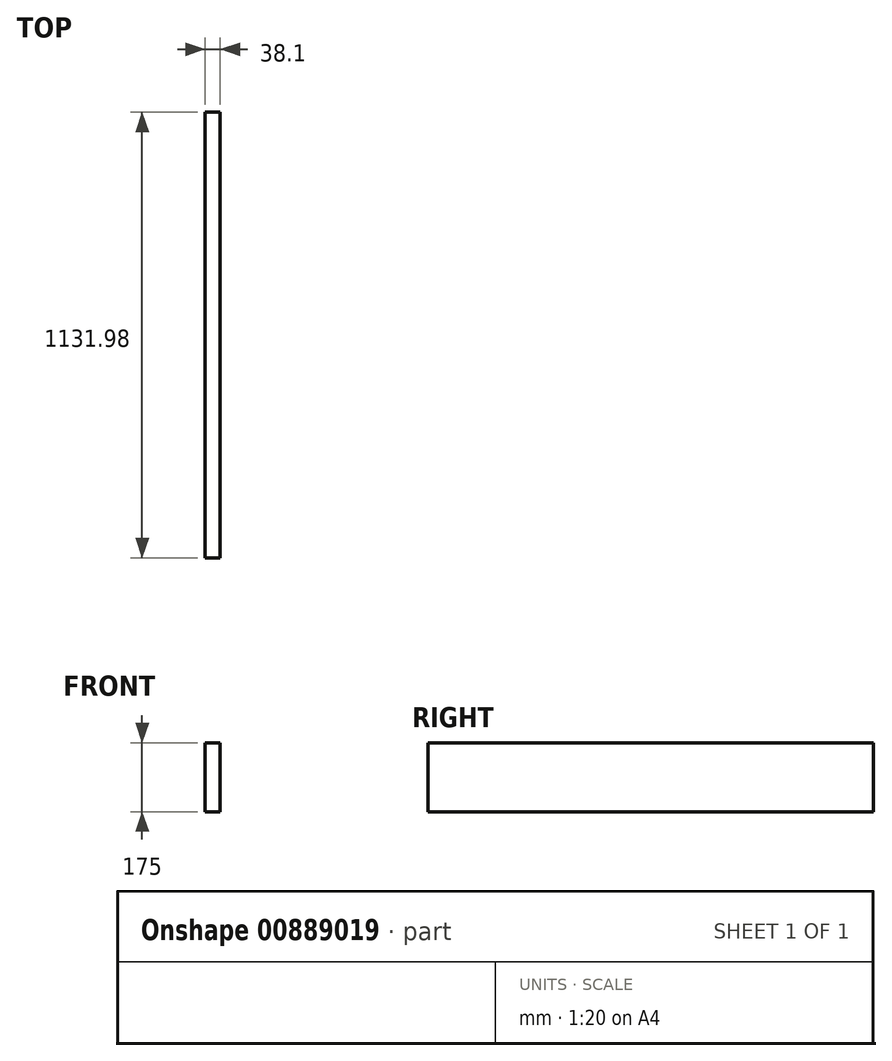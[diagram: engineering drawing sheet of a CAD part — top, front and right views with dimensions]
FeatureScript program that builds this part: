
annotation { "Feature Type Name" : "Feature", "Feature Type Description" : "" }
export const myFeature = defineFeature(function(context is Context, id is Id, definition is map)
    precondition{}
    {
        {
            var Q0;
            Q0=qCreatedBy(makeId("Right.planeOp"),FACE);
            var sketch = newSketch(context, id + "F0", { "sketchPlane" : qUnion([Q0])});
            skLineSegment(sketch, "E0.bottom", {"start": v(0, 0) * mm, "end": v(1131.98, 0) * mm});
            skLineSegment(sketch, "E0.top", {"start": v(0, 175) * mm, "end": v(1131.98, 175) * mm});
            skLineSegment(sketch, "E0.left", {"start": v(0, 0) * mm, "end": v(0, 175) * mm});
            skLineSegment(sketch, "E0.right", {"start": v(1131.98, 0) * mm, "end": v(1131.98, 175) * mm});
            skSolve(sketch);
        }
        {
            var Q0;
            Q0 = qSketchRegion(id + "F0", true);
            extrude(context, id + "F1", {"entities" : qUnion([Q0]), "depth" : 38.1 * mm, "offsetDistance" : 25 * mm});
        }
    });
